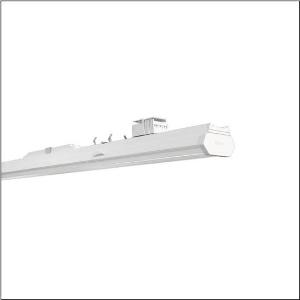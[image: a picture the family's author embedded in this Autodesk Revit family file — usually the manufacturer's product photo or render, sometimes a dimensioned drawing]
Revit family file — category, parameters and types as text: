
# Revit family: licross_11_protected_extreme_ho_51td1bdn4e5me
name_source: partatom
category: Lighting Fixtures
units: mm (PartAtom-declared; Revit-internal decimal feet)

## family parameters
Cut with Voids When Loaded = No
Host = Face
Light Source = No
Part Type = Normal
Room Calculation Point = No
Round Connector Dimension = Use Diameter
Shared = No

## types (1)
- --- (1 x LED, 14500 lm, 87.3 W, 4000K)
    Apparent Load = 87 VA
    CIE Flux Codes = 54 82 95 97 100
    Color Rendering = 80
    Color Temperature = 4000K
    Default Elevation = 1800 mm
    Description = Licross 11 Protected extreme HO, luminaire insert, of sheet steel, galvanised, coil coated, white, length: 1.500mm, width: 90mm, height: 101mm, LED rated luminous flux: 14.500lm, light colour: 840, SDCM (Standard Deviation of Colour Matching)MacAdam ≤ 2 SDCM (initial), control gear: DALI 2, with plug, 5-pole, with phase selection, mains connection: 220..240V, AC, 50/60Hz, rated input power: 87W, internal wiring halogen-free, primary optical cover: cover, of PMMA, light emission: direct distribution, primary light characteristic: symmetric, protection rating (complete): IP54, insulation class (complete): insulation class I (protective earthing), certification: CE, ENEC, VDE, UKCA, protection symbol: D if used in an environment with non-conductive dust loads with corresponding accessories, impact resistance: IK06, permissible ambient temperature for indoor applications: -40..+40°C, corresponds to IFS (International Featured Standards) requirements for safety and quality in the food industry, reducing of maximum allowable ambient temperature of 5°C with ceiling mounting, LABS conformity tested according to VDMA 24364:2018-05, The light source and the operating device comply with the requirements of the Ecodesign Regulation (EU) 2019/2020 and are replaceable in accordance with this regulation, packaging unit: 1 piece
    Height = 92 mm
    Lamp = 1 x LED
    Lamp Light Flux = 14500 lm
    Lamp Power = 87.3 W
    Lamp count = 1
    Length = 1500 mm
    Luminous efficacy = 166 lm/W
    Manufacturer = Siteco
    ModVariant = No
    Model = 51TD1BDN4E5ME
    Mounting Place = Ceiling
    Mounting Type = Pendant
    Number of Poles = 1
    OnlyDefault = Yes
    Power Factor = 1
    Product Name = Licross 11 Protected extreme HO
    Product group = luminaire insert | ceiling pendant
    ProductGroupID = 901
    Protection Class = Protection class I
    Protection Degree = IP 54
    RLX_Detail_Level = 1
    RLX_Emergency_Light_Flux = 0 lm
    RLX_Emergency_Type = 0
    RLX_Emergency_Type_DB = No
    RlxData = <blob elided: 24553 chars, md5=700aeee7>
    Socket = socket
    Standby Power = 0 W
    System Light Flux = 14500 lm
    System Power = 87 W
    Type Comments = factory setting: luminous flux: 100 % | dim-lin: 254 | 589 mA
    Type Image = l_1256145.jpg
    URL = http://relux.com
    VarID = @adj_089507
    Voltage = 0 V
    Weight = 0.00 kg
    Width = 88 mm

## geometry (parser evidence)
native form markers: Blend x4, Sweep x10
no freeform markers — native parametric forms only
